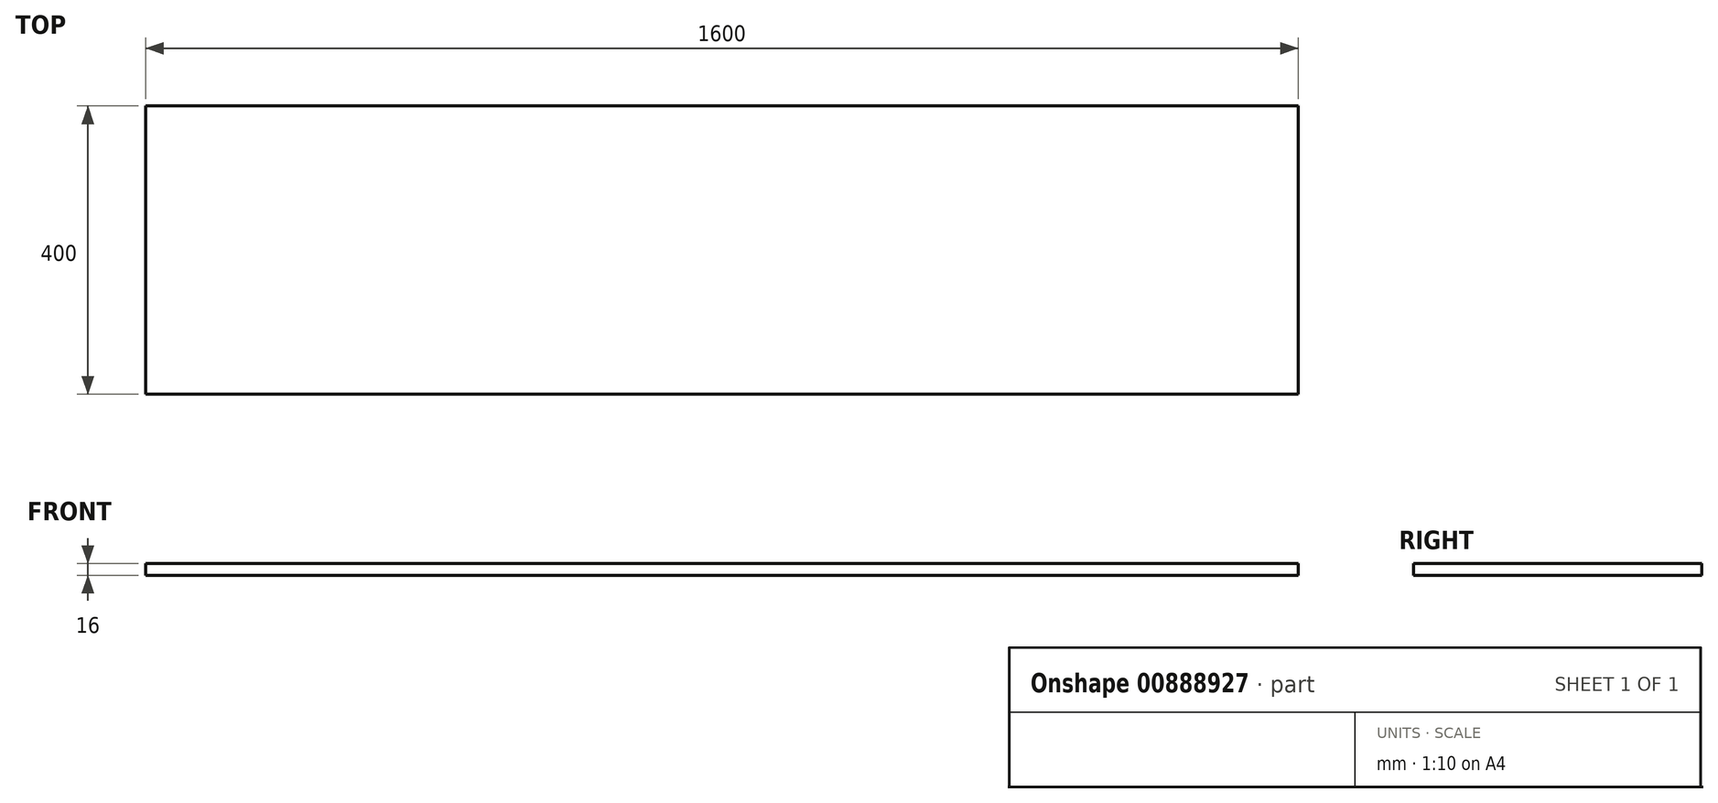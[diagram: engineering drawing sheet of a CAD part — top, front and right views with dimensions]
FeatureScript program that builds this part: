
annotation { "Feature Type Name" : "Feature", "Feature Type Description" : "" }
export const myFeature = defineFeature(function(context is Context, id is Id, definition is map)
    precondition{}
    {
        {
            var Q0;
            Q0=qCreatedBy(makeId("Top.planeOp"),FACE);
            var sketch = newSketch(context, id + "F0", { "sketchPlane" : qUnion([Q0])});
            skLineSegment(sketch, "E0.bottom", {"start": v(800, 200) * mm, "end": v(-800, 200) * mm});
            skLineSegment(sketch, "E0.top", {"start": v(800, -200) * mm, "end": v(-800, -200) * mm});
            skLineSegment(sketch, "E0.left", {"start": v(800, 200) * mm, "end": v(800, -200) * mm});
            skLineSegment(sketch, "E0.right", {"start": v(-800, 200) * mm, "end": v(-800, -200) * mm});
            skPoint(sketch, "E0.middle", {"position": v(0, 0) * mm});
            skSolve(sketch);
        }
        {
            var Q0;
            Q0=makeQuery(id+"F0.imprint","IMPRINT",FACE,{"disambiguationData":[TD([[makeQuery(id+"F0.imprint","IMPRINT",EDGE,{"derivedFrom":sQuery(id+"F0.wireOp",EDGE,"E0.bottom")}),1.0]])]});
            extrude(context, id + "F1", {"entities" : qUnion([Q0]), "depth" : 16 * mm, "offsetDistance" : 25 * mm});
        }
    });
